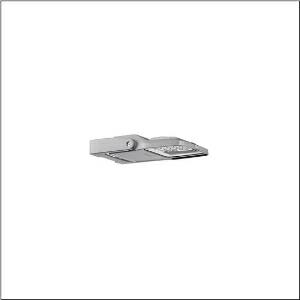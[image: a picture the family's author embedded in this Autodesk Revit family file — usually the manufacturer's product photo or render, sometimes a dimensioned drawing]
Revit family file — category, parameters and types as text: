
# Revit family: floodlight_fl_21_iq_micro___pl33t_5xa7762a2f2a_46b5
name_source: partatom
category: Lighting Fixtures
units: mm (PartAtom-declared; Revit-internal decimal feet)

## family parameters
Cut with Voids When Loaded = No
Host = Face
Light Source = No
Part Type = Normal
Room Calculation Point = No
Round Connector Dimension = Use Diameter
Shared = No

## types (1)
- --- (1 x LED, 2930 lm, 23.1 W, 3000K)
    Apparent Load = 23 VA
    CIE Flux Codes = 26 75 99 100 100
    Color Rendering = 70
    Color Temperature = 3000K
    Default Elevation = 1800 mm
    Description = Floodlight FL 21 iQ micro, floodlight, primary light control with lens, of PMMA, primary optical cover: protective disc, of toughened safety glass, transparent, light distribution: PL33T, light emission: direct distribution, installation type: surface-mounted, LED, High Power LED, rated luminous flux: 2.930lm, luminous efficacy: 127lm/W, light colour: 730, colour temperature: 3000K, control gear: iQ Street-Remote/DALI, control: Auto-Match, Temp-Guard, Night-Set, Smart-Wire, Desk-Remote (wireless, voltage-free reading and setting of iQ features in the workshop via application-optimized NFC function/RFID function), optimised constant luminous flux control (CLO 2.0), Street-Remote, with terminal, 6-pole, mains connection: 220..240V, AC, 50/60Hz, start of lifetime: 23W, end of service life: 24W, reduction: 11W, luminaire housing, of diecast aluminium, powder-coated, Siteco® metallic grey (DB 702S), corrosivity category C5 mid according to DIN EN ISO 12944, suitable for swimming pools, chlorine-resistant, sealing non-destructively replaceable, design bracket, of diecast aluminium, powder-coated, Siteco® metallic grey (DB 702S), protection rating (complete): IP66, insulation class (complete): insulation class II (safety insulation), certification: CE, ENEC, VDE, protection symbol: D, impact resistance: IK07, permissible operating ambient temperature: -40..+40°C, permissible operating ambient temperature for outdoor applications: -40..+50°C, standard: DIN EN 12944, LABS conformity tested according to VDMA 24364:2018-05, packaging unit: 1 piece

Light Distribution: PL33T
    Height = 65 mm
    Lamp = 1 x LED
    Lamp Light Flux = 2930 lm
    Lamp Power = 23.1 W
    Lamp count = 1
    Length = 312 mm
    Luminous efficacy = 127 lm/W
    Manufacturer = Siteco
    ModVariant = No
    Model = 5XA7762A2F2A
    Mounting Place = Wall
    Mounting Type = Surface mounted
    Number of Poles = 1
    OnlyDefault = Yes
    Power Factor = 1
    Product Name = Floodlight FL 21 iQ micro | PL33T
    Product group = floodlight | wall mounted
    ProductGroupID = 2001
    Protection Class = Protection class II
    Protection Degree = IP 66
    RLX_Detail_Level = 1
    RLX_Emergency_Light_Flux = 0 lm
    RLX_Emergency_Type = 0
    RLX_Emergency_Type_DB = No
    RlxData = <blob elided: 97605 chars, md5=cdb1964b>
    Socket = socket
    Standby Power = 0 W
    System Light Flux = 2930 lm
    System Power = 23 W
    Type Comments = factory setting: luminous flux: 100 % | dim-lin: 254 | 455 mA
    Type Image = l_1006878.jpg
    URL = http://relux.com
    VarID = @adj_169443
    Voltage = 0 V
    Weight = 0.00 kg
    Width = 230 mm

## geometry (parser evidence)
native form markers: Blend x4, Sweep x11
no freeform markers — native parametric forms only
